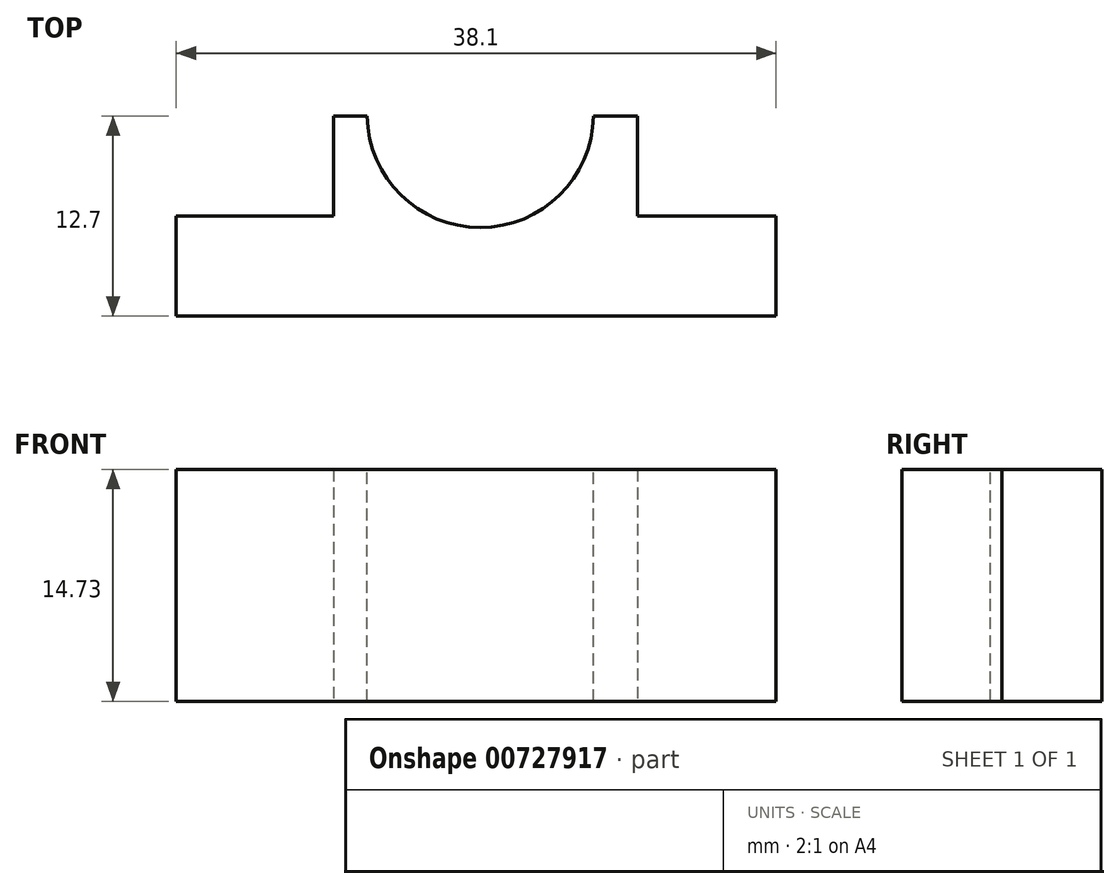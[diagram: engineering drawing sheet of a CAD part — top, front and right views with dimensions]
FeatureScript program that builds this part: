
annotation { "Feature Type Name" : "Feature", "Feature Type Description" : "" }
export const myFeature = defineFeature(function(context is Context, id is Id, definition is map)
    precondition{}
    {
        {
            var Q0;
            Q0=qCreatedBy(makeId("Top.planeOp"),FACE);
            var sketch = newSketch(context, id + "F0", { "sketchPlane" : qUnion([Q0])});
            skLineSegment(sketch, "E0.bottom", {"start": v(-18.5, 3.6) * mm, "end": v(19.6, 3.6) * mm});
            skLineSegment(sketch, "E0.top", {"start": v(-18.5, -2.74) * mm, "end": v(19.6, -2.74) * mm});
            skLineSegment(sketch, "E0.left", {"start": v(-18.5, 3.6) * mm, "end": v(-18.5, -2.74) * mm});
            skLineSegment(sketch, "E0.right", {"start": v(19.6, 3.6) * mm, "end": v(19.6, -2.74) * mm});
            skSolve(sketch);
        }
        {
            var Q0;
            Q0=makeQuery(id+"F0.imprint","IMPRINT",FACE,{"disambiguationData":[TD([[makeQuery(id+"F0.imprint","IMPRINT",EDGE,{"derivedFrom":sQuery(id+"F0.wireOp",EDGE,"E0.bottom")}),-1.0]])]});
            var sketch = newSketch(context, id + "F1", { "sketchPlane" : qUnion([Q0])});
            skLineSegment(sketch, "E1.bottom", {"start": v(-8.49, 3.6) * mm, "end": v(10.81, 3.6) * mm});
            skLineSegment(sketch, "E1.top", {"start": v(-8.49, 9.96) * mm, "end": v(10.81, 9.96) * mm});
            skLineSegment(sketch, "E1.left", {"start": v(-8.49, 3.6) * mm, "end": v(-8.49, 9.96) * mm});
            skLineSegment(sketch, "E1.right", {"start": v(10.81, 3.6) * mm, "end": v(10.81, 9.96) * mm});
            skSolve(sketch);
        }
        {
            var Q0;
            Q0 = qSketchRegion(id + "F1", true);
            extrude(context, id + "F2", {"entities" : qUnion([Q0]), "depth" : 14.73 * mm, "offsetDistance" : 25.4 * mm});
        }
        {
            var Q0;
            Q0=makeQuery(id+"F0.imprint","IMPRINT",FACE,{"disambiguationData":[TD([[makeQuery(id+"F0.imprint","IMPRINT",EDGE,{"derivedFrom":sQuery(id+"F0.wireOp",EDGE,"E0.bottom")}),-1.0]])]});
            extrude(context, id + "F3", {"entities" : qUnion([Q0]), "operationType" : NewBodyOperationType.ADD, "depth" : 14.73 * mm, "offsetDistance" : 25.4 * mm});
        }
        {
            var Q0;
            Q0=makeQuery(id+"F3.boolean.opBoolean","MERGE",FACE,{"derivedFrom":[makeQuery(id+"F2.opExtrude","CAP_FACE",FACE,{"disambiguationData":[OSD([sQuery(id+"F1.wireOp",EDGE,"E1.bottom"),sQuery(id+"F1.wireOp",EDGE,"E1.top"),sQuery(id+"F1.wireOp",EDGE,"E1.left"),sQuery(id+"F1.wireOp",EDGE,"E1.right")])],"isStart":false}),makeQuery(id+"F3.opExtrude","CAP_FACE",FACE,{"disambiguationData":[OSD([sQuery(id+"F0.wireOp",EDGE,"E0.bottom"),sQuery(id+"F0.wireOp",EDGE,"E0.top"),sQuery(id+"F0.wireOp",EDGE,"E0.left"),sQuery(id+"F0.wireOp",EDGE,"E0.right")])],"isStart":false})]});
            var sketch = newSketch(context, id + "F4", { "sketchPlane" : qUnion([Q0])});
            skSolve(sketch);
        }
        {
            var Q0;
            {var subQ3=sQuery(id+"F1.wireOp",EDGE,"E1.top");Q0=makeQuery(id+"F4.imprint","IMPRINT",FACE,{"disambiguationData":[TD([[makeQuery(id+"F4.imprint","IMPRINT",EDGE,{"derivedFrom":makeQuery(id+"F2.opExtrude","CAP_EDGE",EDGE,{"disambiguationData":[OSD([subQ3])],"isStart":false})}),-1.0]])]});}
            var sketch = newSketch(context, id + "F5", { "sketchPlane" : qUnion([Q0])});
            skCircle(sketch, "E2", {"center": v(0.82, 10.07) * mm, "radius": 7.19 * mm});
            skSolve(sketch);
        }
        {
            var Q0;
            Q0 = qSketchRegion(id + "F5", true);
            extrude(context, id + "F6", {"entities" : qUnion([Q0]), "operationType" : NewBodyOperationType.REMOVE, "endBound" : BoundingType.THROUGH_ALL, "oppositeDirection" : true, "depth" : 25.4 * mm, "offsetDistance" : 25.4 * mm});
        }
    });
